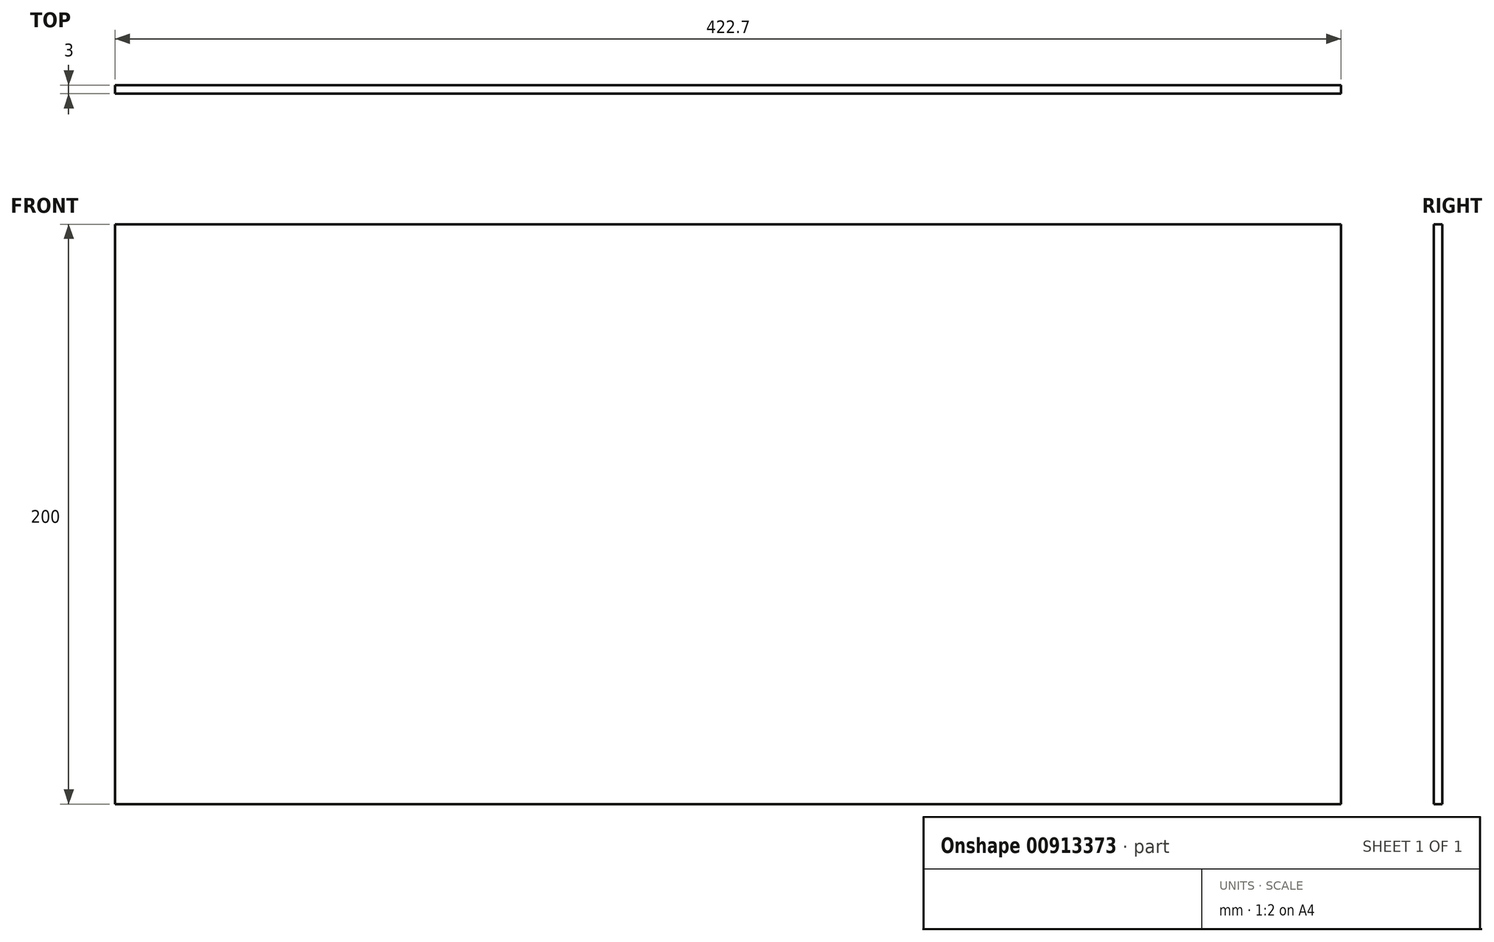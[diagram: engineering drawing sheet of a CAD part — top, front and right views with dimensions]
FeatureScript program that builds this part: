
annotation { "Feature Type Name" : "Feature", "Feature Type Description" : "" }
export const myFeature = defineFeature(function(context is Context, id is Id, definition is map)
    precondition{}
    {
        {
            var Q0;
            Q0=qCreatedBy(makeId("Front.planeOp"),FACE);
            var sketch = newSketch(context, id + "F0", { "sketchPlane" : qUnion([Q0])});
            skLineSegment(sketch, "E0.bottom", {"start": v(-211.35, 100) * mm, "end": v(211.35, 100) * mm});
            skLineSegment(sketch, "E0.top", {"start": v(-211.35, -100) * mm, "end": v(211.35, -100) * mm});
            skLineSegment(sketch, "E0.left", {"start": v(-211.35, 100) * mm, "end": v(-211.35, -100) * mm});
            skLineSegment(sketch, "E0.right", {"start": v(211.35, 100) * mm, "end": v(211.35, -100) * mm});
            skPoint(sketch, "E0.middle", {"position": v(0, 0) * mm});
            skSolve(sketch);
        }
        {
            var Q0;
            Q0=qSketchRegion(id+"F0",true);
            extrude(context, id + "F1", {"entities" : qUnion([Q0]), "depth" : 3 * mm, "offsetDistance" : 25 * mm});
        }
    });
